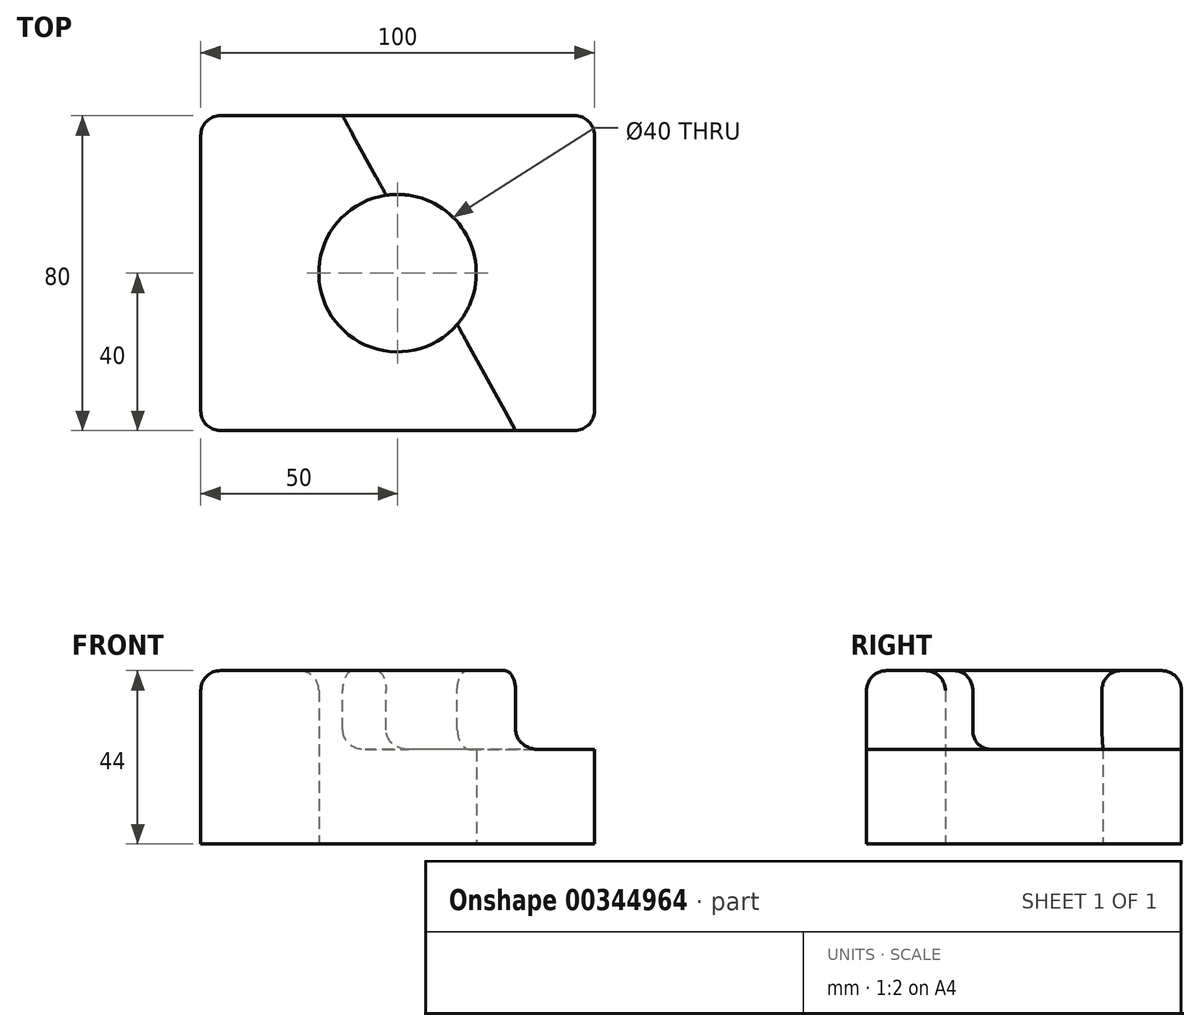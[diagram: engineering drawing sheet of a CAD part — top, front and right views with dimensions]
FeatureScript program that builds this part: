
annotation { "Feature Type Name" : "Feature", "Feature Type Description" : "" }
export const myFeature = defineFeature(function(context is Context, id is Id, definition is map)
    precondition{}
    {
        {
            var Q0;
            Q0=qCreatedBy(makeId("Top.planeOp"),FACE);
            var sketch = newSketch(context, id + "F0", { "sketchPlane" : qUnion([Q0])});
            skLineSegment(sketch, "E0.bottom", {"start": v(50, 40) * mm, "end": v(-50, 40) * mm});
            skLineSegment(sketch, "E0.top", {"start": v(50, -40) * mm, "end": v(-50, -40) * mm});
            skLineSegment(sketch, "E0.left", {"start": v(50, 40) * mm, "end": v(50, -40) * mm});
            skLineSegment(sketch, "E0.right", {"start": v(-50, 40) * mm, "end": v(-50, -40) * mm});
            skPoint(sketch, "E0.middle", {"position": v(0, 0) * mm});
            skCircle(sketch, "E1", {"center": v(0, 0) * mm, "radius": 20 * mm});
            skSolve(sketch);
        }
        {
            var Q0;
            Q0=makeQuery(id+"F0.imprint","IMPRINT",FACE,{"disambiguationData":[TD([[makeQuery(id+"F0.imprint","IMPRINT",EDGE,{"derivedFrom":sQuery(id+"F0.wireOp",EDGE,"E0.bottom")}),1.0]])]});
            extrude(context, id + "F1", {"entities" : qUnion([Q0]), "depth" : 44 * mm});
        }
        {
            var Q0;
            Q0=makeQuery(id+"F1.opExtrude","CAP_FACE",FACE,{"disambiguationData":[OSD([sQuery(id+"F0.wireOp",EDGE,"E0.bottom"),sQuery(id+"F0.wireOp",EDGE,"E0.top"),sQuery(id+"F0.wireOp",EDGE,"E0.left"),sQuery(id+"F0.wireOp",EDGE,"E0.right"),sQuery(id+"F0.wireOp",EDGE,"E1")])],"isStart":false});
            var sketch = newSketch(context, id + "F2", { "sketchPlane" : qUnion([Q0])});
            skLineSegment(sketch, "E2", {"start": v(-14, 40) * mm, "end": v(30, -40) * mm});
            skLineSegment(sketch, "E3.0", {"start": v(50, 40) * mm, "end": v(-14, 40) * mm});
            skLineSegment(sketch, "E4.0", {"start": v(50, 40) * mm, "end": v(50, -40) * mm});
            skLineSegment(sketch, "E5.0", {"start": v(50, -40) * mm, "end": v(30, -40) * mm});
            skPoint(sketch, "E6.orphan", {"position": v(-50, -40) * mm});
            skPoint(sketch, "E7.orphan", {"position": v(-50, 40) * mm});
            skSolve(sketch);
        }
        {
            var Q0;
            {var subQ0=sQuery(id+"F2.wireOp",EDGE,"E3.0");Q0=makeQuery(id+"F2.imprint","IMPRINT",FACE,{"disambiguationData":[TD([[makeQuery(id+"F2.imprint","IMPRINT",EDGE,{"derivedFrom":subQ0}),1.0]])]});}
            extrude(context, id + "F3", {"entities" : qUnion([Q0]), "operationType" : NewBodyOperationType.REMOVE, "oppositeDirection" : true, "depth" : 20 * mm});
        }
        {
            var Q0;
            {var subQ0=sQuery(id+"F2.wireOp",EDGE,"E2");Q0=makeQuery(id+"F3.boolean.opBoolean","COPY",EDGE,{"derivedFrom":makeQuery(id+"F3.opExtrude","CAP_EDGE",EDGE,{"disambiguationData":[OSD([subQ0]),TDD([makeQuery(id+"F2.imprint","IMPRINT",EDGE,{"disambiguationData":[TD([[makeQuery(id+"F2.imprint","INTERSECT",VERTEX,{"disambiguationData":[OD(1.0)],"derivedFrom":[makeQuery(id+"F1.opExtrude","CAP_EDGE",EDGE,{"disambiguationData":[OSD([sQuery(id+"F0.wireOp",EDGE,"E1")])],"isStart":false}),subQ0]}),-1.0]])],"derivedFrom":subQ0})])],"isStart":true})});}
            var Q1;
            Q1=makeQuery(id+"F1.opExtrude","CAP_EDGE",EDGE,{"disambiguationData":[OSD([sQuery(id+"F0.wireOp",EDGE,"E1")])],"isStart":false});
            var Q2;
            {var subQ0=sQuery(id+"F2.wireOp",EDGE,"E2");Q2=makeQuery(id+"F3.boolean.opBoolean","COPY",EDGE,{"derivedFrom":makeQuery(id+"F3.opExtrude","CAP_EDGE",EDGE,{"disambiguationData":[OSD([subQ0]),TDD([makeQuery(id+"F2.imprint","IMPRINT",EDGE,{"disambiguationData":[TD([[makeQuery(id+"F2.imprint","INTERSECT",VERTEX,{"disambiguationData":[OD(0.0)],"derivedFrom":[makeQuery(id+"F1.opExtrude","CAP_EDGE",EDGE,{"disambiguationData":[OSD([sQuery(id+"F0.wireOp",EDGE,"E1")])],"isStart":false}),subQ0]}),1.0]])],"derivedFrom":subQ0})])],"isStart":true})});}
            var Q3;
            {var subQ0=sQuery(id+"F2.wireOp",EDGE,"E2");var subQ1=sQuery(id+"F0.wireOp",EDGE,"E1");Q3=makeQuery(id+"F3.boolean.opBoolean","COPY",EDGE,{"derivedFrom":makeQuery(id+"F3.opExtrude","SWEPT_EDGE",EDGE,{"disambiguationData":[OSD([subQ1,subQ0]),TDD([makeQuery(id+"F2.imprint","INTERSECT",VERTEX,{"disambiguationData":[OD(1.0)],"derivedFrom":[makeQuery(id+"F1.opExtrude","CAP_EDGE",EDGE,{"disambiguationData":[OSD([subQ1])],"isStart":false}),subQ0]})])]})});}
            var Q4;
            {var subQ0=sQuery(id+"F2.wireOp",EDGE,"E2");var subQ1=sQuery(id+"F0.wireOp",EDGE,"E1");Q4=makeQuery(id+"F3.boolean.opBoolean","COPY",EDGE,{"derivedFrom":makeQuery(id+"F3.opExtrude","SWEPT_EDGE",EDGE,{"disambiguationData":[OSD([subQ1,subQ0]),TDD([makeQuery(id+"F2.imprint","INTERSECT",VERTEX,{"disambiguationData":[OD(0.0)],"derivedFrom":[makeQuery(id+"F1.opExtrude","CAP_EDGE",EDGE,{"disambiguationData":[OSD([subQ1])],"isStart":false}),subQ0]})])]})});}
            var Q5;
            Q5=makeQuery(id+"F3.boolean.opBoolean","COPY",EDGE,{"derivedFrom":makeQuery(id+"F3.opExtrude","CAP_EDGE",EDGE,{"disambiguationData":[OSD([sQuery(id+"F0.wireOp",EDGE,"E1")])],"isStart":false})});
            var Q6;
            Q6=makeQuery(id+"F1.opExtrude","CAP_EDGE",EDGE,{"disambiguationData":[OSD([sQuery(id+"F0.wireOp",EDGE,"E0.top")])],"isStart":false});
            var Q7;
            Q7=makeQuery(id+"F1.opExtrude","CAP_EDGE",EDGE,{"disambiguationData":[OSD([sQuery(id+"F0.wireOp",EDGE,"E0.right")])],"isStart":false});
            var Q8;
            Q8=makeQuery(id+"F1.opExtrude","CAP_EDGE",EDGE,{"disambiguationData":[OSD([sQuery(id+"F0.wireOp",EDGE,"E0.bottom")])],"isStart":false});
            var Q9;
            Q9=makeQuery(id+"F3.boolean.opBoolean","COPY",EDGE,{"derivedFrom":makeQuery(id+"F3.opExtrude","CAP_EDGE",EDGE,{"disambiguationData":[OSD([sQuery(id+"F2.wireOp",EDGE,"E3.0")])],"isStart":false})});
            var Q10;
            Q10=makeQuery(id+"F3.boolean.opBoolean","COPY",EDGE,{"derivedFrom":makeQuery(id+"F3.opExtrude","SWEPT_EDGE",EDGE,{"disambiguationData":[OSD([sQuery(id+"F0.wireOp",EDGE,"E0.bottom"),sQuery(id+"F2.wireOp",EDGE,"E2"),sQuery(id+"F2.wireOp",EDGE,"E3.0")])]})});
            var Q11;
            Q11=makeQuery(id+"F3.boolean.opBoolean","COPY",EDGE,{"derivedFrom":makeQuery(id+"F3.opExtrude","SWEPT_EDGE",EDGE,{"disambiguationData":[OSD([sQuery(id+"F0.wireOp",EDGE,"E0.top"),sQuery(id+"F2.wireOp",EDGE,"E2"),sQuery(id+"F2.wireOp",EDGE,"E5.0")])]})});
            var Q12;
            Q12=makeQuery(id+"F3.boolean.opBoolean","COPY",EDGE,{"derivedFrom":makeQuery(id+"F3.opExtrude","CAP_EDGE",EDGE,{"disambiguationData":[OSD([sQuery(id+"F2.wireOp",EDGE,"E4.0")])],"isStart":false})});
            var Q13;
            {var subQ0=sQuery(id+"F2.wireOp",EDGE,"E2");Q13=makeQuery(id+"F3.boolean.opBoolean","COPY",EDGE,{"derivedFrom":makeQuery(id+"F3.opExtrude","CAP_EDGE",EDGE,{"disambiguationData":[OSD([subQ0]),TDD([makeQuery(id+"F2.imprint","IMPRINT",EDGE,{"disambiguationData":[TD([[makeQuery(id+"F2.imprint","INTERSECT",VERTEX,{"disambiguationData":[OD(1.0)],"derivedFrom":[makeQuery(id+"F1.opExtrude","CAP_EDGE",EDGE,{"disambiguationData":[OSD([sQuery(id+"F0.wireOp",EDGE,"E1")])],"isStart":false}),subQ0]}),-1.0]])],"derivedFrom":subQ0})])],"isStart":false})});}
            var Q14;
            {var subQ0=sQuery(id+"F2.wireOp",EDGE,"E2");Q14=makeQuery(id+"F3.boolean.opBoolean","COPY",EDGE,{"derivedFrom":makeQuery(id+"F3.opExtrude","CAP_EDGE",EDGE,{"disambiguationData":[OSD([subQ0]),TDD([makeQuery(id+"F2.imprint","IMPRINT",EDGE,{"disambiguationData":[TD([[makeQuery(id+"F2.imprint","INTERSECT",VERTEX,{"disambiguationData":[OD(0.0)],"derivedFrom":[makeQuery(id+"F1.opExtrude","CAP_EDGE",EDGE,{"disambiguationData":[OSD([sQuery(id+"F0.wireOp",EDGE,"E1")])],"isStart":false}),subQ0]}),1.0]])],"derivedFrom":subQ0})])],"isStart":false})});}
            var Q15;
            Q15=makeQuery(id+"F3.boolean.opBoolean","COPY",EDGE,{"derivedFrom":makeQuery(id+"F3.opExtrude","CAP_EDGE",EDGE,{"disambiguationData":[OSD([sQuery(id+"F2.wireOp",EDGE,"E5.0")])],"isStart":false})});
            var Q16;
            Q16=makeQuery(id+"F1.opExtrude","SWEPT_EDGE",EDGE,{"disambiguationData":[OSD([sQuery(id+"F0.wireOp",EDGE,"E0.top"),sQuery(id+"F0.wireOp",EDGE,"E0.left")])]});
            var Q17;
            Q17=makeQuery(id+"F1.opExtrude","SWEPT_EDGE",EDGE,{"disambiguationData":[OSD([sQuery(id+"F0.wireOp",EDGE,"E0.bottom"),sQuery(id+"F0.wireOp",EDGE,"E0.left")])]});
            var Q18;
            Q18=makeQuery(id+"F1.opExtrude","SWEPT_EDGE",EDGE,{"disambiguationData":[OSD([sQuery(id+"F0.wireOp",EDGE,"E0.bottom"),sQuery(id+"F0.wireOp",EDGE,"E0.right")])]});
            var Q19;
            Q19=makeQuery(id+"F1.opExtrude","SWEPT_EDGE",EDGE,{"disambiguationData":[OSD([sQuery(id+"F0.wireOp",EDGE,"E0.top"),sQuery(id+"F0.wireOp",EDGE,"E0.right")])]});
            fillet(context, id + "F4", {"entities" : qUnion([Q0, Q1, Q2, Q3, Q4, Q5, Q6, Q7, Q8, Q9, Q10, Q11, Q12, Q13, Q14, Q15, Q16, Q17, Q18, Q19]), "radius" : 5 * mm, "tangentPropagation" : true, "allowEdgeOverflow" : false});
        }
    });
